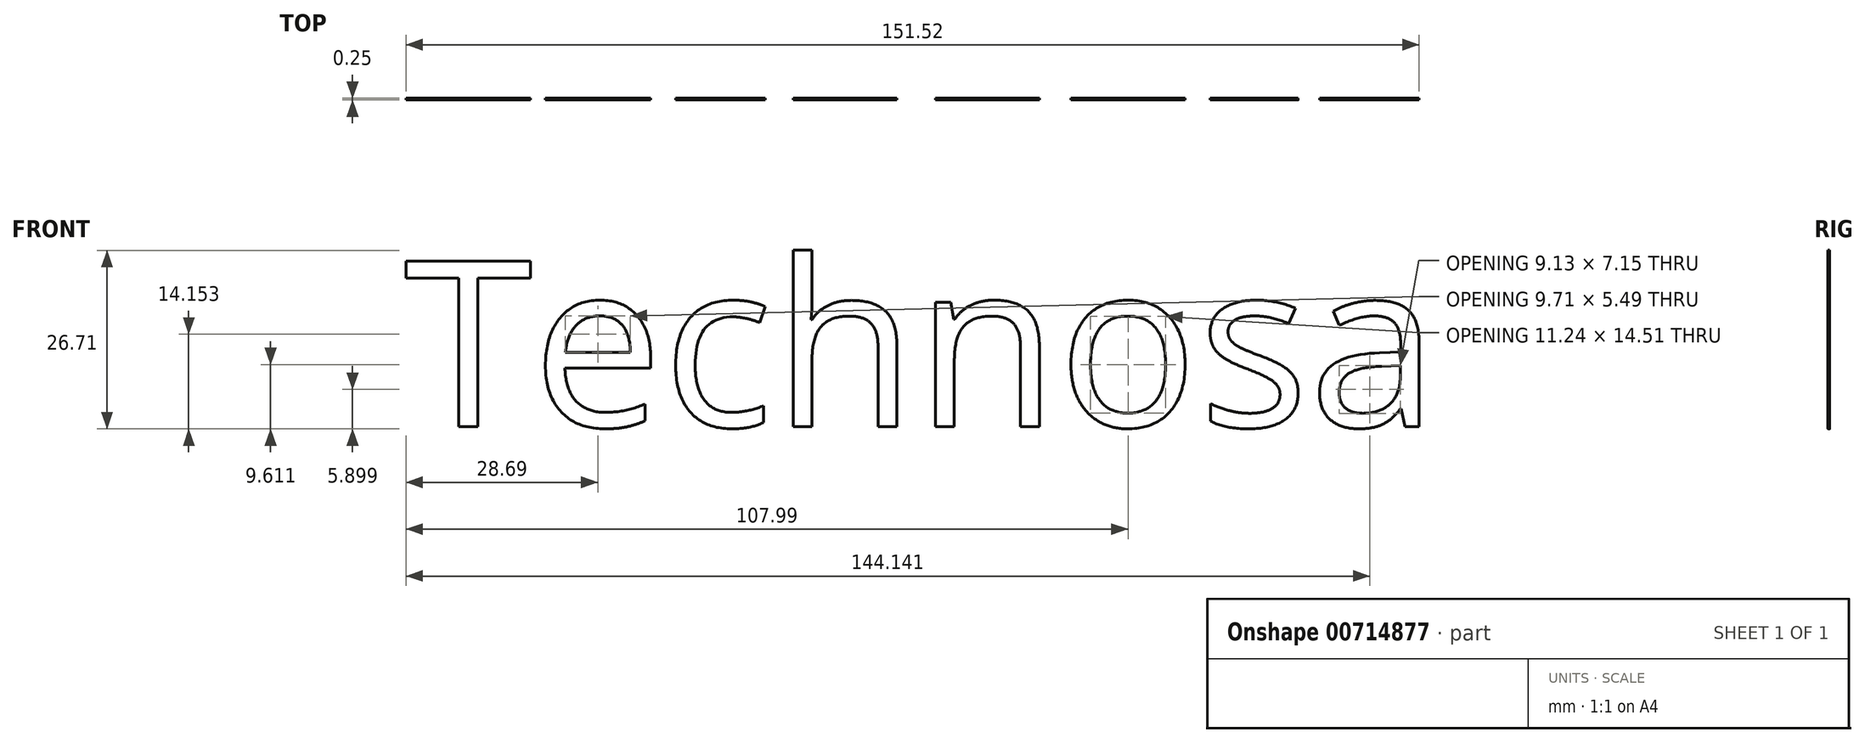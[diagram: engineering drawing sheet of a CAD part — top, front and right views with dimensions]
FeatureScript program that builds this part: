
annotation { "Feature Type Name" : "Feature", "Feature Type Description" : "" }
export const myFeature = defineFeature(function(context is Context, id is Id, definition is map)
    precondition{}
    {
        {
            var Q0;
            Q0=qCreatedBy(makeId("Front.planeOp"),FACE);
            var sketch = newSketch(context, id + "F0", { "sketchPlane" : qUnion([Q0])});
            skText(sketch, "E0", { "text": "Technosa", "fontName": "OpenSans-Regular.ttf"});
            const initialGuessF0  = {"E0": [-0.06357, 0.00515, 1, 0, 0.02499]};
            skSetInitialGuess(sketch, initialGuessF0);
            skSolve(sketch);
        }
        {
            var Q0;
            Q0 = qSketchRegion(id + "F0", true);
            extrude(context, id + "F1", {"entities" : qUnion([Q0]), "depth" : 0.25 * mm, "offsetDistance" : 25.4 * mm});
        }
    });
